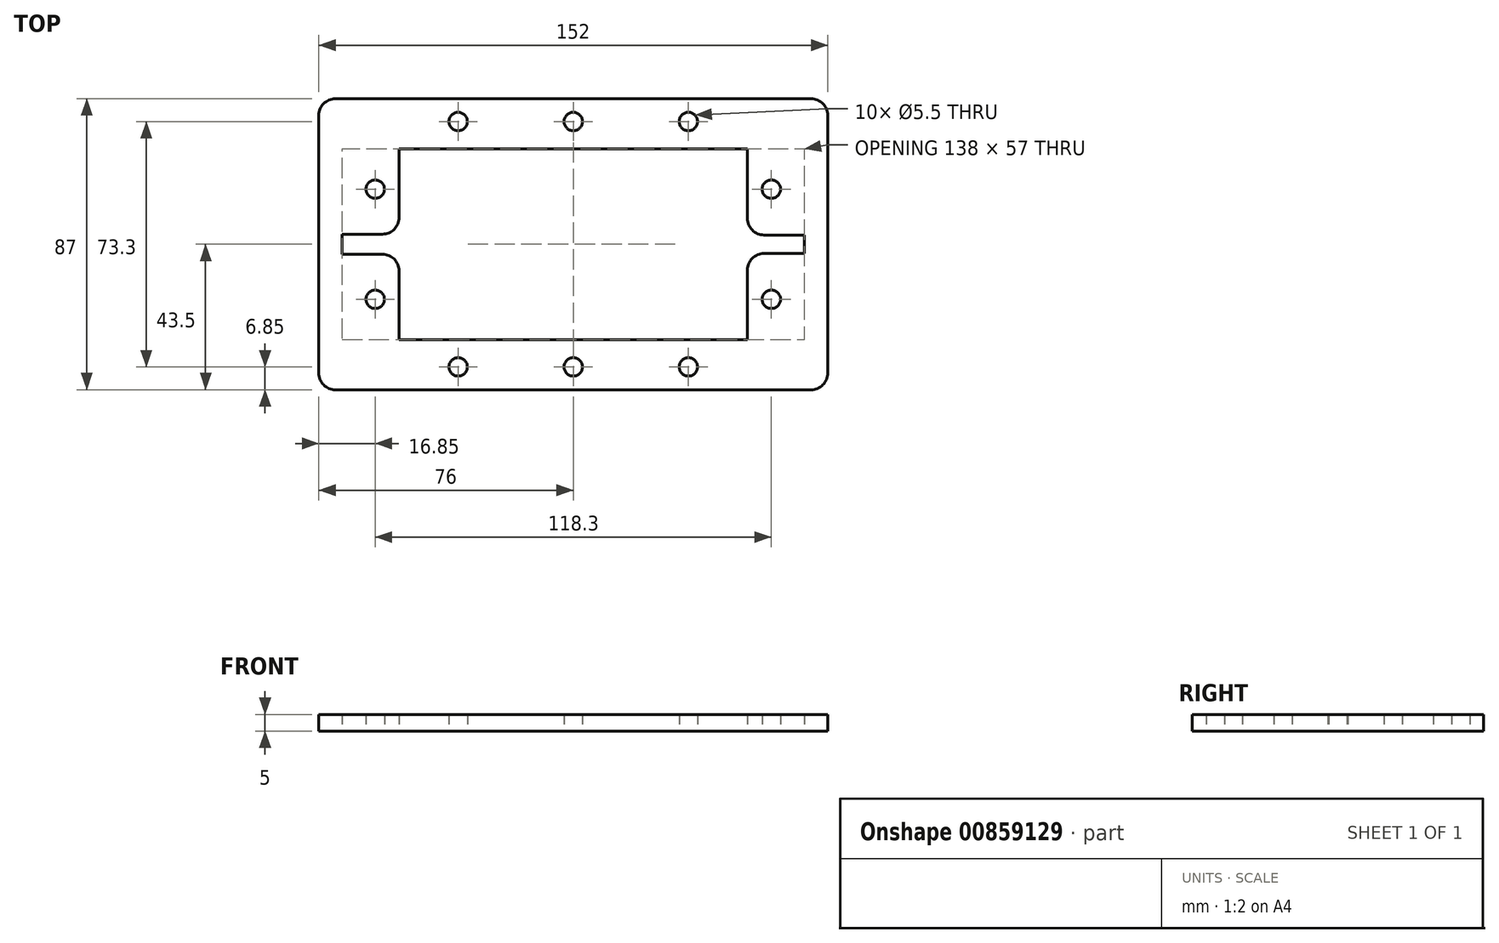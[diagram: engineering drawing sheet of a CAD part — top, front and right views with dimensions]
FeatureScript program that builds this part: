
annotation { "Feature Type Name" : "Feature", "Feature Type Description" : "" }
export const myFeature = defineFeature(function(context is Context, id is Id, definition is map)
    precondition{}
    {
        {
            var Q0;
            Q0=qCreatedBy(makeId("Top.planeOp"),FACE);
            var sketch = newSketch(context, id + "F0", { "sketchPlane" : qUnion([Q0])});
            skLineSegment(sketch, "E0.bottom", {"start": v(0, 0) * mm, "end": v(132, 0) * mm});
            skLineSegment(sketch, "E0.top", {"start": v(0, 57) * mm, "end": v(132, 57) * mm});
            skLineSegment(sketch, "E0.left", {"start": v(0, 0) * mm, "end": v(0, 57) * mm, "construction": true});
            skLineSegment(sketch, "E0.right", {"start": v(132, 0) * mm, "end": v(132, 57) * mm});
            skCircle(sketch, "E1", {"center": v(125.15, 44.95) * mm, "radius": 2.75 * mm});
            skCircle(sketch, "E2", {"center": v(125.15, 12.05) * mm, "radius": 2.75 * mm});
            skLineSegment(sketch, "E3", {"start": v(127.9, 12.05) * mm, "end": v(132, 12.05) * mm, "construction": true});
            skLineSegment(sketch, "E4", {"start": v(127.9, 44.95) * mm, "end": v(132, 44.95) * mm, "construction": true});
            skLineSegment(sketch, "E5", {"start": v(125.15, 14.8) * mm, "end": v(125.15, 25.75) * mm, "construction": true});
            skLineSegment(sketch, "E6", {"start": v(125.15, 47.7) * mm, "end": v(125.15, 57) * mm, "construction": true});
            skLineSegment(sketch, "E7", {"start": v(125.15, 9.3) * mm, "end": v(125.15, 0) * mm, "construction": true});
            skCircle(sketch, "E8", {"center": v(6.85, 44.95) * mm, "radius": 2.75 * mm});
            skCircle(sketch, "E9", {"center": v(6.85, 12.05) * mm, "radius": 2.75 * mm});
            skLineSegment(sketch, "E10", {"start": v(4.1, 12.05) * mm, "end": v(0, 12.05) * mm, "construction": true});
            skLineSegment(sketch, "E11", {"start": v(4.1, 44.95) * mm, "end": v(0, 44.95) * mm, "construction": true});
            skLineSegment(sketch, "E12", {"start": v(6.85, 42.2) * mm, "end": v(6.85, 31.5) * mm, "construction": true});
            skLineSegment(sketch, "E13", {"start": v(6.85, 47.7) * mm, "end": v(6.85, 57) * mm, "construction": true});
            skLineSegment(sketch, "E14", {"start": v(6.85, 9.3) * mm, "end": v(6.85, 0) * mm, "construction": true});
            skLineSegment(sketch, "E15", {"start": v(14, 57) * mm, "end": v(14, 36.5) * mm});
            skLineSegment(sketch, "E16", {"start": v(118, 57) * mm, "end": v(118, 36.25) * mm});
            skLineSegment(sketch, "E17.bottom", {"start": v(0, 57) * mm, "end": v(132, 57) * mm, "construction": true});
            skLineSegment(sketch, "E17.top", {"start": v(0, 72) * mm, "end": v(132, 72) * mm});
            skLineSegment(sketch, "E17.left", {"start": v(0, 57) * mm, "end": v(0, 72) * mm, "construction": true});
            skLineSegment(sketch, "E17.right", {"start": v(132, 57) * mm, "end": v(132, 72) * mm});
            skLineSegment(sketch, "E18.bottom", {"start": v(0, 0) * mm, "end": v(132, 0) * mm, "construction": true});
            skLineSegment(sketch, "E18.top", {"start": v(0, -15) * mm, "end": v(132, -15) * mm});
            skLineSegment(sketch, "E18.left", {"start": v(0, -8.15) * mm, "end": v(0, -15) * mm});
            skLineSegment(sketch, "E18.right", {"start": v(132, 0) * mm, "end": v(132, -15) * mm});
            skCircle(sketch, "E19", {"center": v(31.63, 65.15) * mm, "radius": 2.75 * mm});
            skCircle(sketch, "E20", {"center": v(66, 65.15) * mm, "radius": 2.75 * mm});
            skCircle(sketch, "E21", {"center": v(100.38, 65.15) * mm, "radius": 2.75 * mm});
            skCircle(sketch, "E22", {"center": v(31.63, -8.15) * mm, "radius": 2.75 * mm});
            skCircle(sketch, "E23", {"center": v(66, -8.15) * mm, "radius": 2.75 * mm});
            skCircle(sketch, "E24", {"center": v(100.38, -8.15) * mm, "radius": 2.75 * mm});
            skLineSegment(sketch, "E25", {"start": v(34.38, -8.15) * mm, "end": v(63.25, -8.15) * mm, "construction": true});
            skLineSegment(sketch, "E26", {"start": v(68.75, -8.15) * mm, "end": v(97.63, -8.15) * mm, "construction": true});
            skLineSegment(sketch, "E27", {"start": v(97.63, 65.15) * mm, "end": v(68.75, 65.15) * mm, "construction": true});
            skLineSegment(sketch, "E28", {"start": v(34.38, 65.15) * mm, "end": v(63.25, 65.15) * mm, "construction": true});
            skLineSegment(sketch, "E29", {"start": v(66, 67.9) * mm, "end": v(66, 72) * mm, "construction": true});
            skLineSegment(sketch, "E30", {"start": v(31.63, 67.9) * mm, "end": v(31.63, 72) * mm, "construction": true});
            skLineSegment(sketch, "E31", {"start": v(100.38, 67.9) * mm, "end": v(100.38, 72) * mm});
            skLineSegment(sketch, "E32", {"start": v(100.38, -10.9) * mm, "end": v(100.38, -15) * mm, "construction": true});
            skLineSegment(sketch, "E33", {"start": v(66, -10.9) * mm, "end": v(66, -15) * mm, "construction": true});
            skLineSegment(sketch, "E34", {"start": v(31.63, -10.9) * mm, "end": v(31.63, -15) * mm, "construction": true});
            skLineSegment(sketch, "E35", {"start": v(103.13, 65.15) * mm, "end": v(132, 65.15) * mm, "construction": true});
            skLineSegment(sketch, "E36", {"start": v(28.88, 65.15) * mm, "end": v(0, 65.15) * mm, "construction": true});
            skLineSegment(sketch, "E37", {"start": v(28.88, -8.15) * mm, "end": v(0, -8.15) * mm, "construction": true});
            skLineSegment(sketch, "E38", {"start": v(103.13, -8.15) * mm, "end": v(132, -8.15) * mm, "construction": true});
            skLineSegment(sketch, "E39", {"start": v(135, 28.25) * mm, "end": v(135, 31.25) * mm});
            skLineSegment(sketch, "E40", {"start": v(135, 28.25) * mm, "end": v(135, 25.75) * mm});
            skLineSegment(sketch, "E41", {"start": v(-3, 28.5) * mm, "end": v(-3, 25.5) * mm});
            skLineSegment(sketch, "E42", {"start": v(-3, 28.5) * mm, "end": v(-3, 31.5) * mm});
            skLineSegment(sketch, "E43", {"start": v(-3, 31.5) * mm, "end": v(9, 31.5) * mm});
            skLineSegment(sketch, "E44", {"start": v(-3, 25.5) * mm, "end": v(9, 25.5) * mm});
            skLineSegment(sketch, "E45", {"start": v(135, 31.25) * mm, "end": v(123, 31.25) * mm});
            skLineSegment(sketch, "E46", {"start": v(135, 25.75) * mm, "end": v(123, 25.75) * mm});
            skPoint(sketch, "E47.orphan", {"position": v(118, 28.5) * mm});
            skLineSegment(sketch, "E48.trimOffspring", {"start": v(118, 20.75) * mm, "end": v(118, 0) * mm});
            skLineSegment(sketch, "E49.trimOffspring", {"start": v(14, 20.5) * mm, "end": v(14, 0) * mm});
            skPoint(sketch, "E50.orphan", {"position": v(14, 28.5) * mm});
            skLineSegment(sketch, "E51.trimOffspring", {"start": v(6.85, 25.5) * mm, "end": v(6.85, 14.8) * mm, "construction": true});
            skLineSegment(sketch, "E52.trimOffspring", {"start": v(125.15, 31.25) * mm, "end": v(125.15, 42.2) * mm, "construction": true});
            skLineSegment(sketch, "E53.bottom", {"start": v(0, 57) * mm, "end": v(-10, 57) * mm});
            skLineSegment(sketch, "E53.top", {"start": v(0, 0) * mm, "end": v(-10, 0) * mm});
            skLineSegment(sketch, "E53.left", {"start": v(0, 57) * mm, "end": v(0, 0) * mm});
            skLineSegment(sketch, "E53.right", {"start": v(-10, 57) * mm, "end": v(-10, 0) * mm});
            skLineSegment(sketch, "E54.bottom", {"start": v(132, 57) * mm, "end": v(142, 57) * mm});
            skLineSegment(sketch, "E54.top", {"start": v(132, 0) * mm, "end": v(142, 0) * mm, "construction": true});
            skLineSegment(sketch, "E54.left", {"start": v(132, 57) * mm, "end": v(132, 0) * mm, "construction": true});
            skLineSegment(sketch, "E54.right", {"start": v(142, 57) * mm, "end": v(142, 0) * mm});
            skLineSegment(sketch, "E55.bottom", {"start": v(132, -15) * mm, "end": v(137, -15) * mm});
            skLineSegment(sketch, "E55.top", {"start": v(132, 0) * mm, "end": v(142, 0) * mm});
            skLineSegment(sketch, "E55.left", {"start": v(132, -15) * mm, "end": v(132, 0) * mm, "construction": true});
            skLineSegment(sketch, "E55.right", {"start": v(142, -10) * mm, "end": v(142, 0) * mm});
            skLineSegment(sketch, "E56.bottom", {"start": v(142, 57) * mm, "end": v(132, 57) * mm, "construction": true});
            skLineSegment(sketch, "E56.top", {"start": v(137, 72) * mm, "end": v(132, 72) * mm});
            skLineSegment(sketch, "E56.left", {"start": v(142, 57) * mm, "end": v(142, 67) * mm});
            skLineSegment(sketch, "E56.right", {"start": v(132, 57) * mm, "end": v(132, 72) * mm, "construction": true});
            skLineSegment(sketch, "E57.bottom", {"start": v(0, 72) * mm, "end": v(-5, 72) * mm});
            skLineSegment(sketch, "E57.top", {"start": v(0, 57) * mm, "end": v(-10, 57) * mm, "construction": true});
            skLineSegment(sketch, "E57.left", {"start": v(0, 72) * mm, "end": v(0, 57) * mm});
            skLineSegment(sketch, "E57.right", {"start": v(-10, 67) * mm, "end": v(-10, 57) * mm});
            skLineSegment(sketch, "E58.bottom", {"start": v(-10, 0) * mm, "end": v(0, 0) * mm});
            skLineSegment(sketch, "E58.top", {"start": v(-5, -15) * mm, "end": v(0, -15) * mm});
            skLineSegment(sketch, "E58.left", {"start": v(-10, 0) * mm, "end": v(-10, -10) * mm});
            skLineSegment(sketch, "E58.right", {"start": v(0, 0) * mm, "end": v(0, -15) * mm, "construction": true});
            skPoint(sketch, "E59.visualSharp", {"position": v(-10, 72) * mm});
            skArc(sketch, "E59.filletArc", {"start": v(-5, 72) * mm, "mid": v(-8.54, 70.54) * mm, "end": v(-10, 67) * mm});
            skPoint(sketch, "E60.visualSharp", {"position": v(-10, -15) * mm});
            skArc(sketch, "E60.filletArc", {"start": v(-10, -10) * mm, "mid": v(-8.54, -13.54) * mm, "end": v(-5, -15) * mm});
            skPoint(sketch, "E61.visualSharp", {"position": v(142, -15) * mm});
            skArc(sketch, "E61.filletArc", {"start": v(137, -15) * mm, "mid": v(140.54, -13.54) * mm, "end": v(142, -10) * mm});
            skPoint(sketch, "E62.visualSharp", {"position": v(142, 72) * mm});
            skArc(sketch, "E62.filletArc", {"start": v(142, 67) * mm, "mid": v(140.54, 70.54) * mm, "end": v(137, 72) * mm});
            skPoint(sketch, "E63.visualSharp", {"position": v(14, 31.5) * mm});
            skArc(sketch, "E63.filletArc", {"start": v(9, 31.5) * mm, "mid": v(12.54, 32.96) * mm, "end": v(14, 36.5) * mm});
            skPoint(sketch, "E64.visualSharp", {"position": v(14, 25.5) * mm});
            skArc(sketch, "E64.filletArc", {"start": v(14, 20.5) * mm, "mid": v(12.54, 24.04) * mm, "end": v(9, 25.5) * mm});
            skPoint(sketch, "E65.visualSharp", {"position": v(118, 25.75) * mm});
            skArc(sketch, "E65.filletArc", {"start": v(123, 25.75) * mm, "mid": v(119.46, 24.29) * mm, "end": v(118, 20.75) * mm});
            skPoint(sketch, "E66.visualSharp", {"position": v(118, 31.25) * mm});
            skArc(sketch, "E66.filletArc", {"start": v(118, 36.25) * mm, "mid": v(119.46, 32.71) * mm, "end": v(123, 31.25) * mm});
            skSolve(sketch);
        }
        {
            var Q0;
            {var subQ0=sQuery(id+"F0.wireOp",EDGE,"E17.right");Q0=makeQuery(id+"F0.imprint","IMPRINT",FACE,{"disambiguationData":[TD([[makeQuery(id+"F0.imprint","IMPRINT",EDGE,{"derivedFrom":subQ0}),1.0]])]});}
            var Q1;
            Q1=makeQuery(id+"F0.imprint","IMPRINT",FACE,{"disambiguationData":[TD([[makeQuery(id+"F0.imprint","IMPRINT",EDGE,{"derivedFrom":sQuery(id+"F0.wireOp",EDGE,"E53.bottom")}),-1.0]])]});
            var Q2;
            Q2=makeQuery(id+"F0.imprint","IMPRINT",FACE,{"disambiguationData":[TD([[makeQuery(id+"F0.imprint","IMPRINT",EDGE,{"derivedFrom":sQuery(id+"F0.wireOp",EDGE,"E53.bottom")}),1.0]])]});
            var Q3;
            Q3=makeQuery(id+"F0.imprint","IMPRINT",FACE,{"disambiguationData":[TD([[makeQuery(id+"F0.imprint","IMPRINT",EDGE,{"derivedFrom":sQuery(id+"F0.wireOp",EDGE,"E18.top")}),1.0]])]});
            var Q4;
            Q4=makeQuery(id+"F0.imprint","IMPRINT",FACE,{"disambiguationData":[TD([[makeQuery(id+"F0.imprint","IMPRINT",EDGE,{"derivedFrom":sQuery(id+"F0.wireOp",EDGE,"E18.right")}),1.0]])]});
            var Q5;
            Q5=makeQuery(id+"F0.imprint","IMPRINT",FACE,{"disambiguationData":[TD([[makeQuery(id+"F0.imprint","IMPRINT",EDGE,{"derivedFrom":sQuery(id+"F0.wireOp",EDGE,"E0.right")}),-1.0]])]});
            var Q6;
            Q6=makeQuery(id+"F0.imprint","IMPRINT",FACE,{"disambiguationData":[TD([[makeQuery(id+"F0.imprint","IMPRINT",EDGE,{"derivedFrom":sQuery(id+"F0.wireOp",EDGE,"E17.right")}),-1.0]])]});
            var Q7;
            {var subQ0=sQuery(id+"F0.wireOp",EDGE,"E0.right");Q7=makeQuery(id+"F0.imprint","IMPRINT",FACE,{"disambiguationData":[TD([[makeQuery(id+"F0.imprint","IMPRINT",EDGE,{"derivedFrom":subQ0}),1.0]])]});}
            var Q8;
            Q8=makeQuery(id+"F0.imprint","IMPRINT",FACE,{"disambiguationData":[TD([[makeQuery(id+"F0.imprint","IMPRINT",EDGE,{"derivedFrom":sQuery(id+"F0.wireOp",EDGE,"E8")}),-1.0]])]});
            var Q9;
            Q9=makeQuery(id+"F0.imprint","IMPRINT",FACE,{"disambiguationData":[TD([[makeQuery(id+"F0.imprint","IMPRINT",EDGE,{"derivedFrom":sQuery(id+"F0.wireOp",EDGE,"E9")}),-1.0]])]});
            extrude(context, id + "F1", {"entities" : qUnion([Q0, Q1, Q2, Q3, Q4, Q5, Q6, Q7, Q8, Q9]), "depth" : 5 * mm, "offsetDistance" : 25 * mm});
        }
    });
